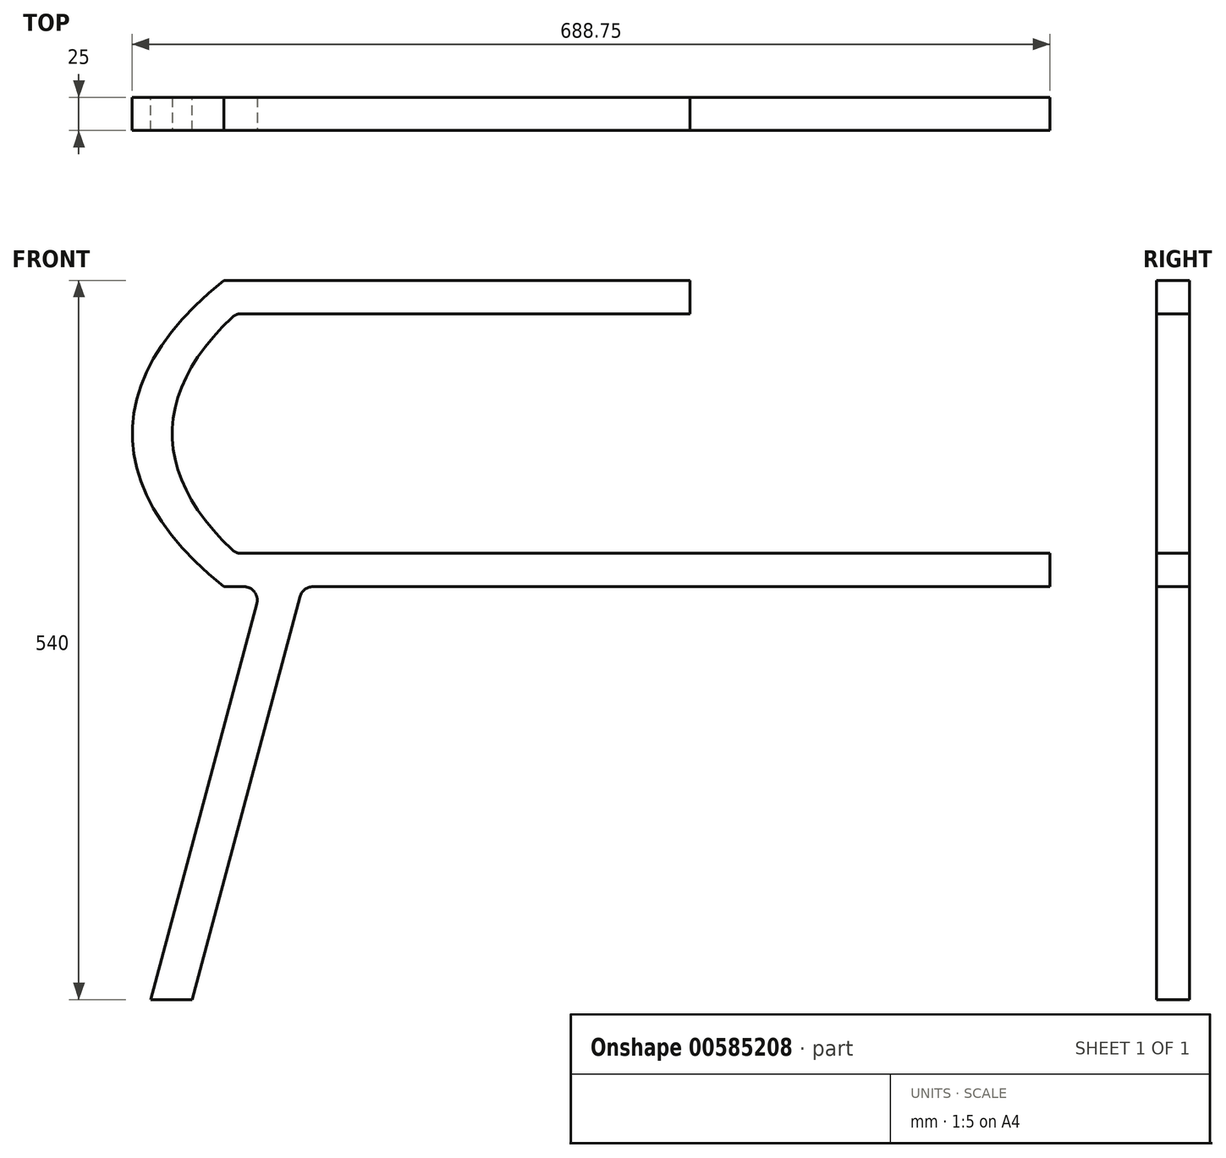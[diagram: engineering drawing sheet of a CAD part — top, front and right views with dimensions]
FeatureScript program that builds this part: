
annotation { "Feature Type Name" : "Feature", "Feature Type Description" : "" }
export const myFeature = defineFeature(function(context is Context, id is Id, definition is map)
    precondition{}
    {
        {
            var Q0;
            Q0=qCreatedBy(makeId("Front.planeOp"),FACE);
            var sketch = newSketch(context, id + "F0", { "sketchPlane" : qUnion([Q0])});
            skLineSegment(sketch, "E0", {"start": v(0, 0) * mm, "end": v(620, 0) * mm});
            skLineSegment(sketch, "E1", {"start": v(620, 25) * mm, "end": v(620, 0) * mm});
            skLineSegment(sketch, "E2", {"start": v(620, 25) * mm, "end": v(9.16, 25) * mm});
            skEllipse(sketch, "E3", {"center": v(831.25, 115) * mm, "majorRadius": 900 * mm, "minorRadius": 300 * mm, "majorAxis": v(-1, 0)});
            skEllipse(sketch, "E4", {"center": v(831.25, 115) * mm, "majorRadius": 870 * mm, "minorRadius": 275 * mm, "majorAxis": v(-1, 0)});
            skLineSegment(sketch, "E5", {"start": v(831.25, 115) * mm, "end": v(-68.75, 115) * mm, "construction": true});
            skLineSegment(sketch, "E6", {"start": v(-38.75, 115) * mm, "end": v(-68.75, 115) * mm, "construction": true});
            skLineSegment(sketch, "E7", {"start": v(831.25, 115) * mm, "end": v(831.25, -185) * mm, "construction": true});
            skLineSegment(sketch, "E8", {"start": v(831.25, -160) * mm, "end": v(831.25, -185) * mm, "construction": true});
            skLineSegment(sketch, "E9", {"start": v(0, 0) * mm, "end": v(0, 115) * mm, "construction": true});
            skLineSegment(sketch, "E10", {"start": v(0, 115) * mm, "end": v(0, 230) * mm, "construction": true});
            skLineSegment(sketch, "E11", {"start": v(0, 230) * mm, "end": v(350, 230) * mm});
            skLineSegment(sketch, "E12", {"start": v(350, 205) * mm, "end": v(350, 230) * mm});
            skLineSegment(sketch, "E13", {"start": v(350, 205) * mm, "end": v(9.16, 205) * mm});
            skLineSegment(sketch, "E14", {"start": v(28.13, 0) * mm, "end": v(-54.94, -310) * mm});
            skLineSegment(sketch, "E15", {"start": v(-54.94, -310) * mm, "end": v(-23.88, -310) * mm});
            skLineSegment(sketch, "E16", {"start": v(-23.88, -310) * mm, "end": v(59.18, 0) * mm});
            skSolve(sketch);
        }
        {
            var Q0;
            {var subQ4=sQuery(id+"F0.wireOp",EDGE,"E12");Q0=makeQuery(id+"F0.imprint","IMPRINT",FACE,{"disambiguationData":[TD([[makeQuery(id+"F0.imprint","IMPRINT",EDGE,{"derivedFrom":subQ4}),1.0]])]});}
            var Q1;
            {var subQ5=sQuery(id+"F0.wireOp",EDGE,"E0");var subQ7=sQuery(id+"F0.wireOp",EDGE,"E3");var subQ8=makeQuery(id+"F0.imprint","INTERSECT",VERTEX,{"derivedFrom":[subQ5,subQ7]});Q1=makeQuery(id+"F0.imprint","IMPRINT",FACE,{"disambiguationData":[TD([[makeQuery(id+"F0.imprint","IMPRINT",EDGE,{"disambiguationData":[TD([[subQ8,-1.0]])],"derivedFrom":subQ5}),1.0]])]});}
            var Q2;
            {var subQ0=sQuery(id+"F0.wireOp",EDGE,"E1");Q2=makeQuery(id+"F0.imprint","IMPRINT",FACE,{"disambiguationData":[TD([[makeQuery(id+"F0.imprint","IMPRINT",EDGE,{"derivedFrom":subQ0}),-1.0]])]});}
            var Q3;
            {var subQ0=sQuery(id+"F0.wireOp",EDGE,"E14");var subQ1=sQuery(id+"F0.wireOp",EDGE,"E0");var subQ2=makeQuery(id+"F0.imprint","INTERSECT",VERTEX,{"derivedFrom":[subQ1,subQ0]});Q3=makeQuery(id+"F0.imprint","IMPRINT",FACE,{"disambiguationData":[TD([[makeQuery(id+"F0.imprint","IMPRINT",EDGE,{"disambiguationData":[TD([[subQ2,-1.0]])],"derivedFrom":subQ1}),-1.0]])]});}
            var Q4;
            {var subQ0=sQuery(id+"F0.wireOp",EDGE,"E14");var subQ1=sQuery(id+"F0.wireOp",EDGE,"E3");var subQ2=makeQuery(id+"F0.imprint","INTERSECT",VERTEX,{"derivedFrom":[subQ1,subQ0]});Q4=makeQuery(id+"F0.imprint","IMPRINT",FACE,{"disambiguationData":[TD([[makeQuery(id+"F0.imprint","IMPRINT",EDGE,{"disambiguationData":[TD([[subQ2,-1.0]])],"derivedFrom":subQ1}),1.0]])]});}
            var Q5;
            {var subQ5=sQuery(id+"F0.wireOp",EDGE,"E15");Q5=makeQuery(id+"F0.imprint","IMPRINT",FACE,{"disambiguationData":[TD([[makeQuery(id+"F0.imprint","IMPRINT",EDGE,{"derivedFrom":subQ5}),1.0]])]});}
            var Q6;
            {var subQ0=sQuery(id+"F0.wireOp",EDGE,"E16");var subQ1=sQuery(id+"F0.wireOp",EDGE,"E0");var subQ2=makeQuery(id+"F0.imprint","INTERSECT",VERTEX,{"derivedFrom":[subQ1,subQ0]});Q6=makeQuery(id+"F0.imprint","IMPRINT",FACE,{"disambiguationData":[TD([[makeQuery(id+"F0.imprint","IMPRINT",EDGE,{"disambiguationData":[TD([[subQ2,1.0]])],"derivedFrom":subQ1}),-1.0]])]});}
            extrude(context, id + "F1", {"entities" : qUnion([Q0, Q1, Q2, Q3, Q4, Q5, Q6]), "endBound" : BoundingType.SYMMETRIC, "depth" : 25 * mm, "offsetDistance" : 25 * mm});
        }
        {
            var Q0;
            Q0=makeQuery(id+"F1.opExtrude","SWEPT_EDGE",EDGE,{"disambiguationData":[OSD([sQuery(id+"F0.wireOp",EDGE,"E2"),sQuery(id+"F0.wireOp",EDGE,"E4")])]});
            var Q1;
            Q1=makeQuery(id+"F1.opExtrude","SWEPT_EDGE",EDGE,{"disambiguationData":[OSD([sQuery(id+"F0.wireOp",EDGE,"E4"),sQuery(id+"F0.wireOp",EDGE,"E13")])]});
            var Q2;
            Q2=makeQuery(id+"F1.opExtrude","SWEPT_EDGE",EDGE,{"disambiguationData":[OSD([sQuery(id+"F0.wireOp",EDGE,"E0"),sQuery(id+"F0.wireOp",EDGE,"E16")])]});
            var Q3;
            Q3=makeQuery(id+"F1.opExtrude","SWEPT_EDGE",EDGE,{"disambiguationData":[OSD([sQuery(id+"F0.wireOp",EDGE,"E0"),sQuery(id+"F0.wireOp",EDGE,"E14")])]});
            fillet(context, id + "F2", {"entities" : qUnion([Q0, Q1, Q2, Q3]), "radius" : 10 * mm, "tangentPropagation" : true, "allowEdgeOverflow" : false});
        }
    });
